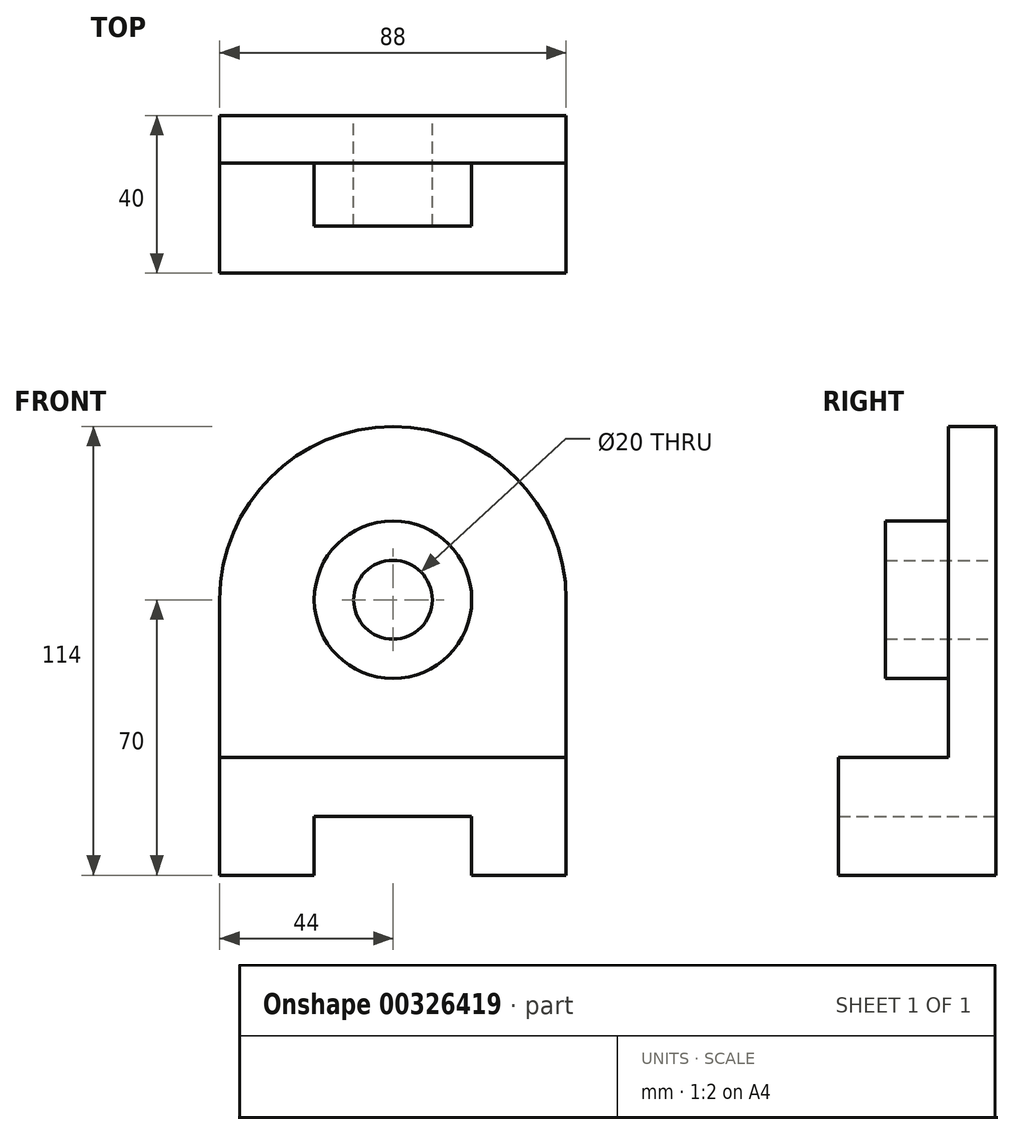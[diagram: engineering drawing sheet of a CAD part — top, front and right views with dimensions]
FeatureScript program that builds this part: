
annotation { "Feature Type Name" : "Feature", "Feature Type Description" : "" }
export const myFeature = defineFeature(function(context is Context, id is Id, definition is map)
    precondition{}
    {
        {
            var Q0;
            Q0=qCreatedBy(makeId("Front.planeOp"),FACE);
            var sketch = newSketch(context, id + "F0", { "sketchPlane" : qUnion([Q0])});
            skLineSegment(sketch, "E0", {"start": v(0, 44) * mm, "end": v(0, -55) * mm, "construction": true});
            skLineSegment(sketch, "E1", {"start": v(-47.34, 0) * mm, "end": v(53.81, 0) * mm, "construction": true});
            skCircle(sketch, "E2", {"center": v(0, 0) * mm, "radius": 10 * mm});
            skCircle(sketch, "E3", {"center": v(0, 0) * mm, "radius": 20 * mm});
            skLineSegment(sketch, "E4", {"start": v(0, -55) * mm, "end": v(-20, -55) * mm});
            skLineSegment(sketch, "E5", {"start": v(-20, -55) * mm, "end": v(-20, -70) * mm});
            skLineSegment(sketch, "E6", {"start": v(-20, -70) * mm, "end": v(-44, -70) * mm});
            skLineSegment(sketch, "E7", {"start": v(-44, -70) * mm, "end": v(-44, 0) * mm});
            skLineSegment(sketch, "E8", {"start": v(-44, -40) * mm, "end": v(0, -40) * mm});
            skLineSegment(sketch, "E9.MirrorCS", {"start": v(44, -70) * mm, "end": v(44, 0) * mm});
            skLineSegment(sketch, "E10.MirrorCS", {"start": v(44, -40) * mm, "end": v(0, -40) * mm});
            skLineSegment(sketch, "E11.MirrorCS", {"start": v(20, -70) * mm, "end": v(44, -70) * mm});
            skLineSegment(sketch, "E12.MirrorCS", {"start": v(0, -55) * mm, "end": v(20, -55) * mm});
            skLineSegment(sketch, "E13.MirrorCS", {"start": v(20, -55) * mm, "end": v(20, -70) * mm});
            skArc(sketch, "E14", {"start": v(44, 0) * mm, "mid": v(0, 44) * mm, "end": v(-44, 0) * mm});
            skSolve(sketch);
        }
        {
            var Q0;
            Q0=makeQuery(id+"F0.imprint","IMPRINT",FACE,{"disambiguationData":[TD([[makeQuery(id+"F0.imprint","IMPRINT",EDGE,{"derivedFrom":sQuery(id+"F0.wireOp",EDGE,"E4")}),-1.0]])]});
            extrude(context, id + "F1", {"entities" : qUnion([Q0]), "depth" : 40 * mm});
        }
        {
            var Q0;
            Q0 = qSketchRegion(id + "F0", true);
            extrude(context, id + "F2", {"entities" : qUnion([Q0]), "operationType" : NewBodyOperationType.ADD, "depth" : 12 * mm});
        }
        {
            var Q0;
            Q0=makeQuery(id+"F0.imprint","IMPRINT",FACE,{"disambiguationData":[TD([[makeQuery(id+"F0.imprint","IMPRINT",EDGE,{"derivedFrom":sQuery(id+"F0.wireOp",EDGE,"E2")}),-1.0]])]});
            extrude(context, id + "F3", {"entities" : qUnion([Q0]), "operationType" : NewBodyOperationType.ADD, "depth" : 28 * mm});
        }
    });
